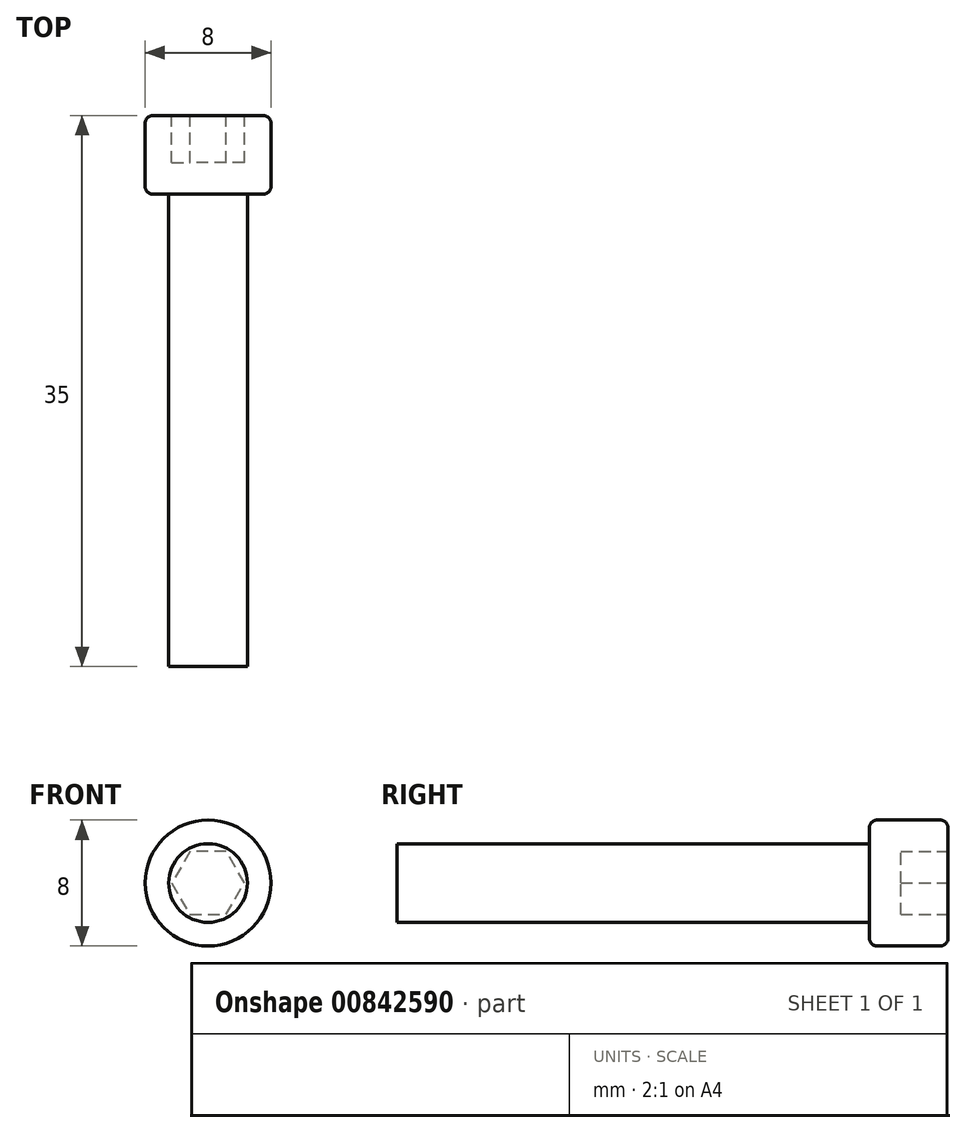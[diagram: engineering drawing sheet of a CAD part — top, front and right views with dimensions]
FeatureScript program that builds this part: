
annotation { "Feature Type Name" : "Feature", "Feature Type Description" : "" }
export const myFeature = defineFeature(function(context is Context, id is Id, definition is map)
    precondition{}
    {
        {
            var Q0;
            Q0=qCreatedBy(makeId("Front.planeOp"),FACE);
            var sketch = newSketch(context, id + "F0", { "sketchPlane" : qUnion([Q0])});
            skCircle(sketch, "E0", {"center": v(0, 0) * mm, "radius": 2.5 * mm});
            skSolve(sketch);
        }
        {
            var Q0;
            Q0 = qSketchRegion(id + "F0", true);
            extrude(context, id + "F1", {"entities" : qUnion([Q0]), "oppositeDirection" : true, "depth" : 30 * mm, "offsetDistance" : 25 * mm});
        }
        {
            var Q0;
            Q0=makeQuery(id+"F1.opExtrude","CAP_FACE",FACE,{"disambiguationData":[OSD([sQuery(id+"F0.wireOp",EDGE,"E0")])],"isStart":false});
            var sketch = newSketch(context, id + "F2", { "sketchPlane" : qUnion([Q0])});
            skCircle(sketch, "E1", {"center": v(0, 0) * mm, "radius": 4 * mm});
            skSolve(sketch);
        }
        {
            var Q0;
            Q0 = qSketchRegion(id + "F2", true);
            extrude(context, id + "F3", {"entities" : qUnion([Q0]), "operationType" : NewBodyOperationType.ADD, "depth" : 5 * mm, "offsetDistance" : 25 * mm});
        }
        {
            var Q0;
            Q0=makeQuery(id+"F3.opExtrude","CAP_EDGE",EDGE,{"disambiguationData":[OSD([sQuery(id+"F2.wireOp",EDGE,"E1")])],"isStart":true});
            var Q1;
            Q1=makeQuery(id+"F3.opExtrude","CAP_EDGE",EDGE,{"disambiguationData":[OSD([sQuery(id+"F2.wireOp",EDGE,"E1")])],"isStart":false});
            fillet(context, id + "F4", {"entities" : qUnion([Q0, Q1]), "radius" : 0.5 * mm, "tangentPropagation" : true, "allowEdgeOverflow" : false});
        }
        {
            var Q0;
            Q0=makeQuery(id+"F3.opExtrude","CAP_FACE",FACE,{"disambiguationData":[OSD([sQuery(id+"F2.wireOp",EDGE,"E1")])],"isStart":false});
            var sketch = newSketch(context, id + "F5", { "sketchPlane" : qUnion([Q0])});
            skCircle(sketch, "E2.cCircle", {"center": v(0, 0) * mm, "radius": 2 * mm, "construction": true});
            skLineSegment(sketch, "E2.0", {"start": v(-1.15, 2) * mm, "end": v(1.15, 2) * mm});
            skLineSegment(sketch, "E2.1", {"start": v(1.15, 2) * mm, "end": v(2.3, 0) * mm});
            skLineSegment(sketch, "E2.2", {"start": v(2.3, 0) * mm, "end": v(1.15, -2) * mm});
            skLineSegment(sketch, "E2.3", {"start": v(1.15, -2) * mm, "end": v(-1.15, -2) * mm});
            skLineSegment(sketch, "E2.4", {"start": v(-1.15, -2) * mm, "end": v(-2.3, 0) * mm});
            skLineSegment(sketch, "E2.5", {"start": v(-2.3, 0) * mm, "end": v(-1.15, 2) * mm});
            skPoint(sketch, "E2.0.midPoint", {"position": v(0, 2) * mm});
            skSolve(sketch);
        }
        {
            var Q0;
            Q0 = qSketchRegion(id + "F5", true);
            extrude(context, id + "F6", {"entities" : qUnion([Q0]), "operationType" : NewBodyOperationType.REMOVE, "oppositeDirection" : true, "depth" : 3 * mm, "offsetDistance" : 25 * mm});
        }
    });
